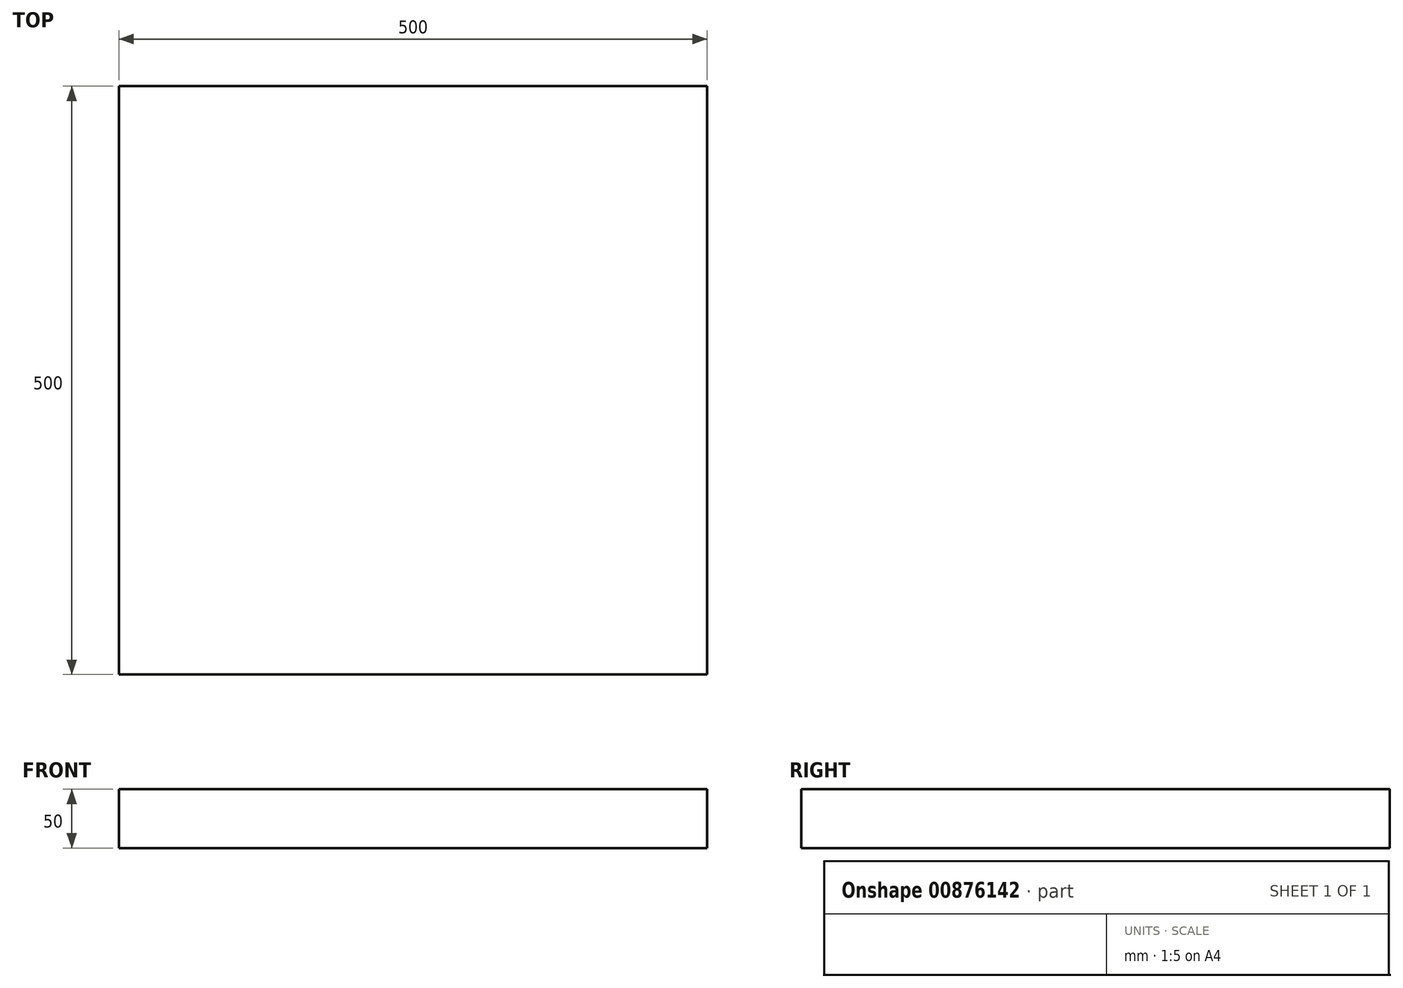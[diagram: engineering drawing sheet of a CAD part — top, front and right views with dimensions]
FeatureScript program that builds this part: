
annotation { "Feature Type Name" : "Feature", "Feature Type Description" : "" }
export const myFeature = defineFeature(function(context is Context, id is Id, definition is map)
    precondition{}
    {
        {
            var Q0;
            Q0=qCreatedBy(makeId("Front.planeOp"),FACE);
            var sketch = newSketch(context, id + "F0", { "sketchPlane" : qUnion([Q0])});
            skLineSegment(sketch, "E0.bottom", {"start": v(-132.5, 0) * mm, "end": v(367.5, 0) * mm});
            skLineSegment(sketch, "E0.top", {"start": v(-132.5, 50) * mm, "end": v(367.5, 50) * mm});
            skLineSegment(sketch, "E0.left", {"start": v(-132.5, 0) * mm, "end": v(-132.5, 50) * mm});
            skLineSegment(sketch, "E0.right", {"start": v(367.5, 0) * mm, "end": v(367.5, 50) * mm});
            skLineSegment(sketch, "E1.bottom", {"start": v(122.5, 50) * mm, "end": v(132.5, 50) * mm});
            skLineSegment(sketch, "E1.top", {"start": v(122.5, 170) * mm, "end": v(132.5, 170) * mm});
            skLineSegment(sketch, "E1.left", {"start": v(132.5, 50) * mm, "end": v(132.5, 170) * mm});
            skLineSegment(sketch, "E1.right", {"start": v(122.5, 50) * mm, "end": v(122.5, 170) * mm});
            skLineSegment(sketch, "E2.bottom", {"start": v(112.98, 50) * mm, "end": v(142.98, 50) * mm});
            skLineSegment(sketch, "E2.top", {"start": v(112.98, 53) * mm, "end": v(142.98, 53) * mm});
            skLineSegment(sketch, "E2.left", {"start": v(112.98, 50) * mm, "end": v(112.98, 53) * mm});
            skLineSegment(sketch, "E2.right", {"start": v(142.98, 50) * mm, "end": v(142.98, 53) * mm});
            skLineSegment(sketch, "E3.bottom", {"start": v(116.72, 61.9) * mm, "end": v(139.04, 61.9) * mm});
            skLineSegment(sketch, "E3.top", {"start": v(116.72, 53) * mm, "end": v(139.04, 53) * mm});
            skLineSegment(sketch, "E3.left", {"start": v(116.72, 61.9) * mm, "end": v(116.72, 53) * mm});
            skLineSegment(sketch, "E3.right", {"start": v(139.04, 61.9) * mm, "end": v(139.04, 53) * mm});
            skSolve(sketch);
        }
        {
            var Q0;
            Q0=makeQuery(id+"F0.imprint","IMPRINT",FACE,{"disambiguationData":[TD([[makeQuery(id+"F0.imprint","IMPRINT",EDGE,{"derivedFrom":sQuery(id+"F0.wireOp",EDGE,"E0.bottom")}),1.0]])]});
            extrude(context, id + "F1", {"entities" : qUnion([Q0]), "depth" : 500 * mm, "offsetDistance" : 25 * mm});
        }
    });
